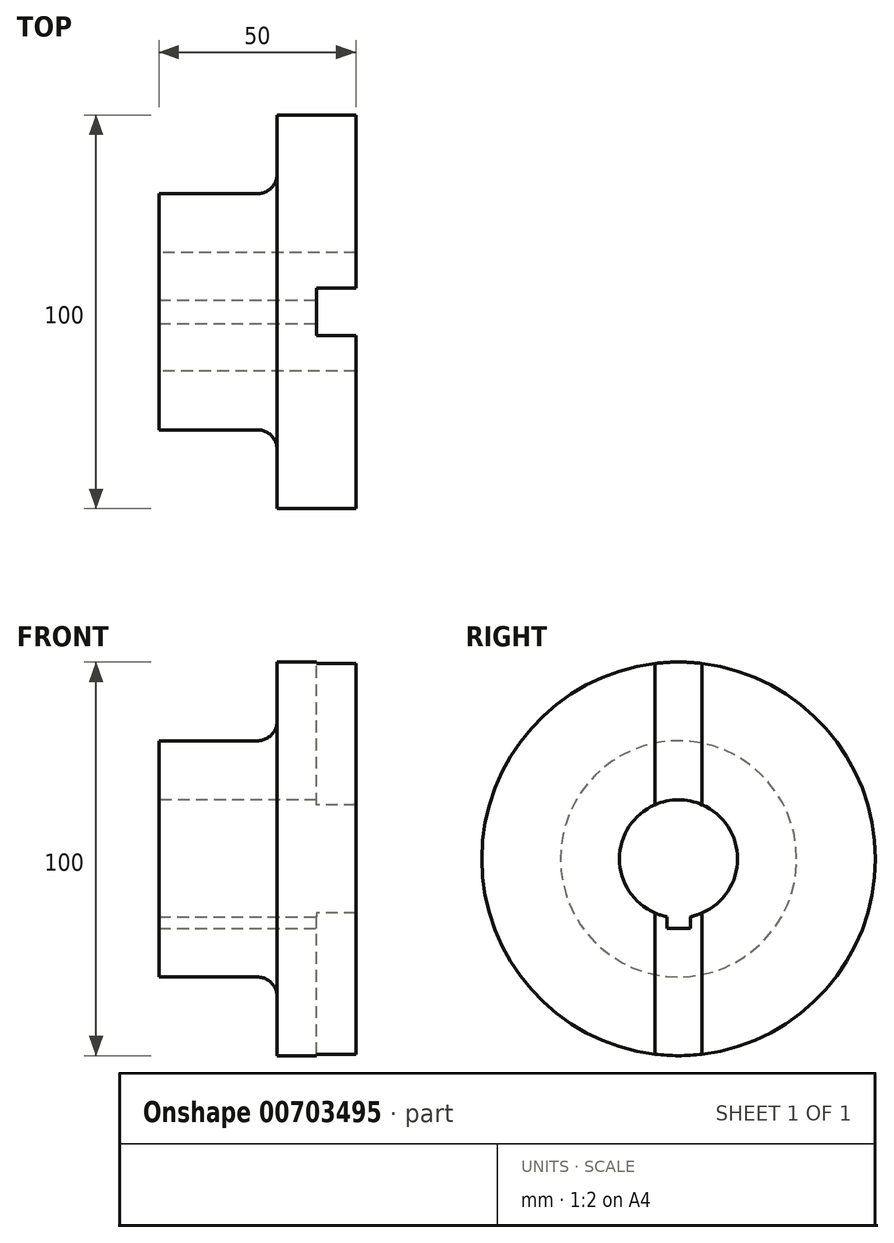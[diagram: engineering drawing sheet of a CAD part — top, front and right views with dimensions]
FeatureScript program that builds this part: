
annotation { "Feature Type Name" : "Feature", "Feature Type Description" : "" }
export const myFeature = defineFeature(function(context is Context, id is Id, definition is map)
    precondition{}
    {
        {
            var Q0;
            Q0=qCreatedBy(makeId("Top.planeOp"),FACE);
            var sketch = newSketch(context, id + "F0", { "sketchPlane" : qUnion([Q0])});
            skLineSegment(sketch, "E0.bottom", {"start": v(0, 0) * mm, "end": v(-50, 0) * mm});
            skLineSegment(sketch, "E0.top", {"start": v(-25, 15) * mm, "end": v(-50, 15) * mm});
            skLineSegment(sketch, "E0.left", {"start": v(0, 0) * mm, "end": v(0, 15) * mm});
            skLineSegment(sketch, "E0.right", {"start": v(-50, 0) * mm, "end": v(-50, 15) * mm});
            skLineSegment(sketch, "E1.bottom", {"start": v(0, 0) * mm, "end": v(-20, 0) * mm});
            skLineSegment(sketch, "E1.top", {"start": v(0, 35) * mm, "end": v(-20, 35) * mm});
            skLineSegment(sketch, "E1.left", {"start": v(0, 0) * mm, "end": v(0, 35) * mm});
            skLineSegment(sketch, "E1.right", {"start": v(-20, 20) * mm, "end": v(-20, 35) * mm});
            skPoint(sketch, "E2.newPointA", {"position": v(-20, 0) * mm});
            skPoint(sketch, "E2.newPointB", {"position": v(0, 15) * mm});
            skArc(sketch, "E2.filletArc", {"start": v(-25, 15) * mm, "mid": v(-21.46, 16.46) * mm, "end": v(-20, 20) * mm});
            skLineSegment(sketch, "E3.bottom", {"start": v(-50, 0) * mm, "end": v(0, 0) * mm});
            skLineSegment(sketch, "E3.top", {"start": v(-50, -15) * mm, "end": v(-10, -15) * mm});
            skLineSegment(sketch, "E3.left", {"start": v(-50, 0) * mm, "end": v(-50, -15) * mm});
            skLineSegment(sketch, "E3.right", {"start": v(0, 0) * mm, "end": v(0, -9) * mm});
            skLineSegment(sketch, "E4.bottom", {"start": v(-10, -9) * mm, "end": v(0, -9) * mm});
            skLineSegment(sketch, "E4.left", {"start": v(-10, -9) * mm, "end": v(-10, -15) * mm});
            skPoint(sketch, "E4.middle", {"position": v(0, -15) * mm});
            skPoint(sketch, "E4.right.start.orphan", {"position": v(10, -9) * mm});
            skPoint(sketch, "E4.top.end.orphan", {"position": v(10, -21) * mm});
            skPoint(sketch, "E5.orphan", {"position": v(-10, -21) * mm});
            skLineSegment(sketch, "E6.top", {"start": v(-10, -21) * mm, "end": v(0, -21) * mm});
            skLineSegment(sketch, "E6.left", {"start": v(-10, -9) * mm, "end": v(-10, -21) * mm});
            skLineSegment(sketch, "E6.right", {"start": v(0, -9) * mm, "end": v(0, -21) * mm});
            skSolve(sketch);
        }
        {
            var Q0;
            Q0=makeQuery(id+"F0.imprint","IMPRINT",FACE,{"disambiguationData":[TD([[makeQuery(id+"F0.imprint","IMPRINT",EDGE,{"derivedFrom":sQuery(id+"F0.wireOp",EDGE,"E0.top")}),1.0]])]});
            var Q1;
            {var subQ1=sQuery(id+"F0.wireOp",EDGE,"E3.top");Q1=makeQuery(id+"F0.imprint","IMPRINT",FACE,{"disambiguationData":[TD([[makeQuery(id+"F0.imprint","IMPRINT",EDGE,{"derivedFrom":subQ1}),1.0]])]});}
            var Q2;
            Q2=sQuery(id+"F0.wireOp",EDGE,"E3.top");
            revolve(context, id + "F1", {"surfaceOperationType" : NewSurfaceOperationType.NEW, "entities" : qUnion([Q0, Q1]), "axis" : qUnion([Q2]), "revolveType" : RevolveType.FULL});
        }
        {
            var Q0;
            {var subQ3=sQuery(id+"F0.wireOp",EDGE,"E4.bottom");Q0=makeQuery(id+"F0.imprint","IMPRINT",FACE,{"disambiguationData":[TD([[makeQuery(id+"F0.imprint","IMPRINT",EDGE,{"derivedFrom":subQ3}),-1.0]])]});}
            extrude(context, id + "F2", {"entities" : qUnion([Q0]), "operationType" : NewBodyOperationType.REMOVE, "endBound" : BoundingType.THROUGH_ALL, "oppositeDirection" : true, "depth" : 25 * mm, "offsetDistance" : 25 * mm, "hasSecondDirection" : true, "secondDirectionBound" : SecondDirectionBoundingType.THROUGH_ALL, "secondDirectionOppositeDirection" : false, "secondDirectionDepth" : 25 * mm});
        }
        {
            var Q0;
            Q0=makeQuery(id+"F1.opRevolve","SWEPT_FACE",FACE,{"disambiguationData":[OSD([sQuery(id+"F0.wireOp",EDGE,"E0.right"),sQuery(id+"F0.wireOp",EDGE,"E3.left")])]});
            var sketch = newSketch(context, id + "F3", { "sketchPlane" : qUnion([Q0])});
            skCircle(sketch, "E7", {"center": v(15, 0) * mm, "radius": 15 * mm});
            skSolve(sketch);
        }
        {
            var Q0;
            Q0=makeQuery(id+"F3.imprint","IMPRINT",FACE,{"disambiguationData":[TD([[makeQuery(id+"F3.imprint","IMPRINT",EDGE,{"derivedFrom":sQuery(id+"F3.wireOp",EDGE,"E7")}),1.0]])]});
            extrude(context, id + "F4", {"entities" : qUnion([Q0]), "operationType" : NewBodyOperationType.REMOVE, "endBound" : BoundingType.THROUGH_ALL, "oppositeDirection" : true, "depth" : 25 * mm, "offsetDistance" : 25 * mm});
        }
        {
            var Q0;
            Q0=makeQuery(id+"F2.boolean.opBoolean","SPLIT",FACE,{"disambiguationData":[TD([makeQuery(id+"F2.opExtrude","SWEPT_FACE",FACE,{"disambiguationData":[OSD([sQuery(id+"F0.wireOp",EDGE,"E6.top")])]})])],"derivedFrom":makeQuery(id+"F1.opRevolve","SWEPT_FACE",FACE,{"disambiguationData":[OSD([sQuery(id+"F0.wireOp",EDGE,"E1.left"),sQuery(id+"F0.wireOp",EDGE,"E3.right")])]})});
            var sketch = newSketch(context, id + "F5", { "sketchPlane" : qUnion([Q0])});
            skCircle(sketch, "E8", {"center": v(-15, 0) * mm, "radius": 15 * mm});
            skLineSegment(sketch, "E9", {"start": v(-32.7, 0) * mm, "end": v(-32.7, 3) * mm});
            skLineSegment(sketch, "E10", {"start": v(-32.7, 3) * mm, "end": v(-29.7, 3) * mm});
            skLineSegment(sketch, "E11", {"start": v(-32.7, 0) * mm, "end": v(-32.7, -3) * mm});
            skLineSegment(sketch, "E12", {"start": v(-32.7, -3) * mm, "end": v(-29.7, -3) * mm});
            skPoint(sketch, "E13.orphan", {"position": v(-30, 0) * mm});
            skPoint(sketch, "E14.end.orphan", {"position": v(-65, 0) * mm});
            skLineSegment(sketch, "E15", {"start": v(-29.7, 3) * mm, "end": v(-29.7, -3) * mm});
            skLineSegment(sketch, "E16.1.0", {"start": v(-18, -17.7) * mm, "end": v(-18, -14.7) * mm});
            skLineSegment(sketch, "E16.1.1", {"start": v(-15, -17.7) * mm, "end": v(-18, -17.7) * mm});
            skLineSegment(sketch, "E16.1.2", {"start": v(-15, -17.7) * mm, "end": v(-12, -17.7) * mm});
            skLineSegment(sketch, "E16.1.3", {"start": v(-12, -17.7) * mm, "end": v(-12, -14.7) * mm});
            skLineSegment(sketch, "E16.1.4", {"start": v(-18, -14.7) * mm, "end": v(-12, -14.7) * mm});
            skLineSegment(sketch, "E16.2.0", {"start": v(2.7, -3) * mm, "end": v(-0.3, -3) * mm});
            skLineSegment(sketch, "E16.2.1", {"start": v(2.7, 0) * mm, "end": v(2.7, -3) * mm});
            skLineSegment(sketch, "E16.2.2", {"start": v(2.7, 0) * mm, "end": v(2.7, 3) * mm});
            skLineSegment(sketch, "E16.2.3", {"start": v(2.7, 3) * mm, "end": v(-0.3, 3) * mm});
            skLineSegment(sketch, "E16.2.4", {"start": v(-0.3, -3) * mm, "end": v(-0.3, 3) * mm});
            skLineSegment(sketch, "E16.3.0", {"start": v(-12, 17.7) * mm, "end": v(-12, 14.7) * mm});
            skLineSegment(sketch, "E16.3.1", {"start": v(-15, 17.7) * mm, "end": v(-12, 17.7) * mm});
            skLineSegment(sketch, "E16.3.2", {"start": v(-15, 17.7) * mm, "end": v(-18, 17.7) * mm});
            skLineSegment(sketch, "E16.3.3", {"start": v(-18, 17.7) * mm, "end": v(-18, 14.7) * mm});
            skLineSegment(sketch, "E16.3.4", {"start": v(-12, 14.7) * mm, "end": v(-18, 14.7) * mm});
            skSolve(sketch);
        }
        {
            var Q0;
            {var subQ1=sQuery(id+"F5.wireOp",EDGE,"E16.1.0");Q0=makeQuery(id+"F5.imprint","IMPRINT",FACE,{"disambiguationData":[TD([[makeQuery(id+"F5.imprint","IMPRINT",EDGE,{"derivedFrom":subQ1}),-1.0]])]});}
            extrude(context, id + "F6", {"entities" : qUnion([Q0]), "operationType" : NewBodyOperationType.REMOVE, "endBound" : BoundingType.THROUGH_ALL, "oppositeDirection" : true, "depth" : 25 * mm, "offsetDistance" : 25 * mm});
        }
    });
